# Revit family: Haworth_Planes_CollaborativeTable_Pebble_AP_PRELIMINARY
name_source: partatom
category: Furniture
units: mm (PartAtom-declared; Revit-internal decimal feet)

## family parameters
Always vertical = Yes
Cut with Voids When Loaded = No
OmniClass Number = 23.40.70.14.64.21
OmniClass Title = Systems Furniture
Room Calculation Point = No
Shared = No
Work Plane-Based = No

## types (6) — shared parameters
Actual Height = 740 mm  [stored 2.42782 ft]
Assembly Code = E2020200
Caster Finish = Haworth _ Polymer _ Black
Description = Haworth - Planes - Collaborative Table - Pebble
Flip Top Finish = Haworth _ Paint _ Undecided _ Table
Leg Height = 715 mm  [stored 2.3458 ft]
Manufacturer = Haworth
Max. Depth = 900 mm  [stored 2.95276 ft]
Max. Width = 1800 mm  [stored 5.90551 ft]
Min. Depth = 750 mm  [stored 2.46063 ft]
Min. Width = 1500 mm  [stored 4.92126 ft]
Model = WOPLTAP
Revision Number = 1
Size = Verify Final Dim. w/ Haworth
Trim Finish = Haworth _ Polymer _ Undecided
URL = https://www.haworth.com
URL - Product = https://www.haworth.com
Warranty = http://www.haworth.com

## per-type parameters (varying)
| type | Actual Depth | Actual Width | Casters | Depth | Flip Top | Glides | Large | Screen Width | Small | Width |
| 1500w x 750d | 750 mm  [stored 2.46063 ft] | 1500 mm  [stored 4.92126 ft] | Yes | 750 mm  [stored 2.46063 ft] | No | No | No | 1000 mm  [stored 3.28084 ft] | Yes | 1500 mm  [stored 4.92126 ft] |
| 1500w x 900d | 900 mm  [stored 2.95276 ft] | 1500 mm  [stored 4.92126 ft] | No | 900 mm  [stored 2.95276 ft] | Yes | Yes | Yes | 1000 mm  [stored 3.28084 ft] | No | 1500 mm  [stored 4.92126 ft] |
| 1600w x 750d | 750 mm  [stored 2.46063 ft] | 1600 mm  [stored 5.24934 ft] | No | 750 mm  [stored 2.46063 ft] | No | Yes | No | 1100 mm | Yes | 1600 mm  [stored 5.24934 ft] |
| 1600w x 900d | 900 mm  [stored 2.95276 ft] | 1600 mm  [stored 5.24934 ft] | Yes | 900 mm  [stored 2.95276 ft] | No | No | Yes | 1100 mm | No | 1600 mm  [stored 5.24934 ft] |
| 1800w x 750d | 750 mm  [stored 2.46063 ft] | 1800 mm  [stored 5.90551 ft] | No | 750 mm  [stored 2.46063 ft] | No | Yes | No | 1300 mm  [stored 4.26509 ft] | Yes | 1800 mm  [stored 5.90551 ft] |
| 1800w x 900d | 900 mm  [stored 2.95276 ft] | 1800 mm  [stored 5.90551 ft] | Yes | 900 mm  [stored 2.95276 ft] | Yes | No | Yes | 1300 mm  [stored 4.26509 ft] | No | 1800 mm  [stored 5.90551 ft] |

type visibility flags: 6 boolean params named "<type name>" — each type sets only its own to Yes (folded from table)

note: [stored X ft] marks values corroborated as IEEE doubles in the binary element streams (Revit-internal decimal feet)

## geometry (parser evidence)
native form markers: Sweep x23
no freeform markers — native parametric forms only
